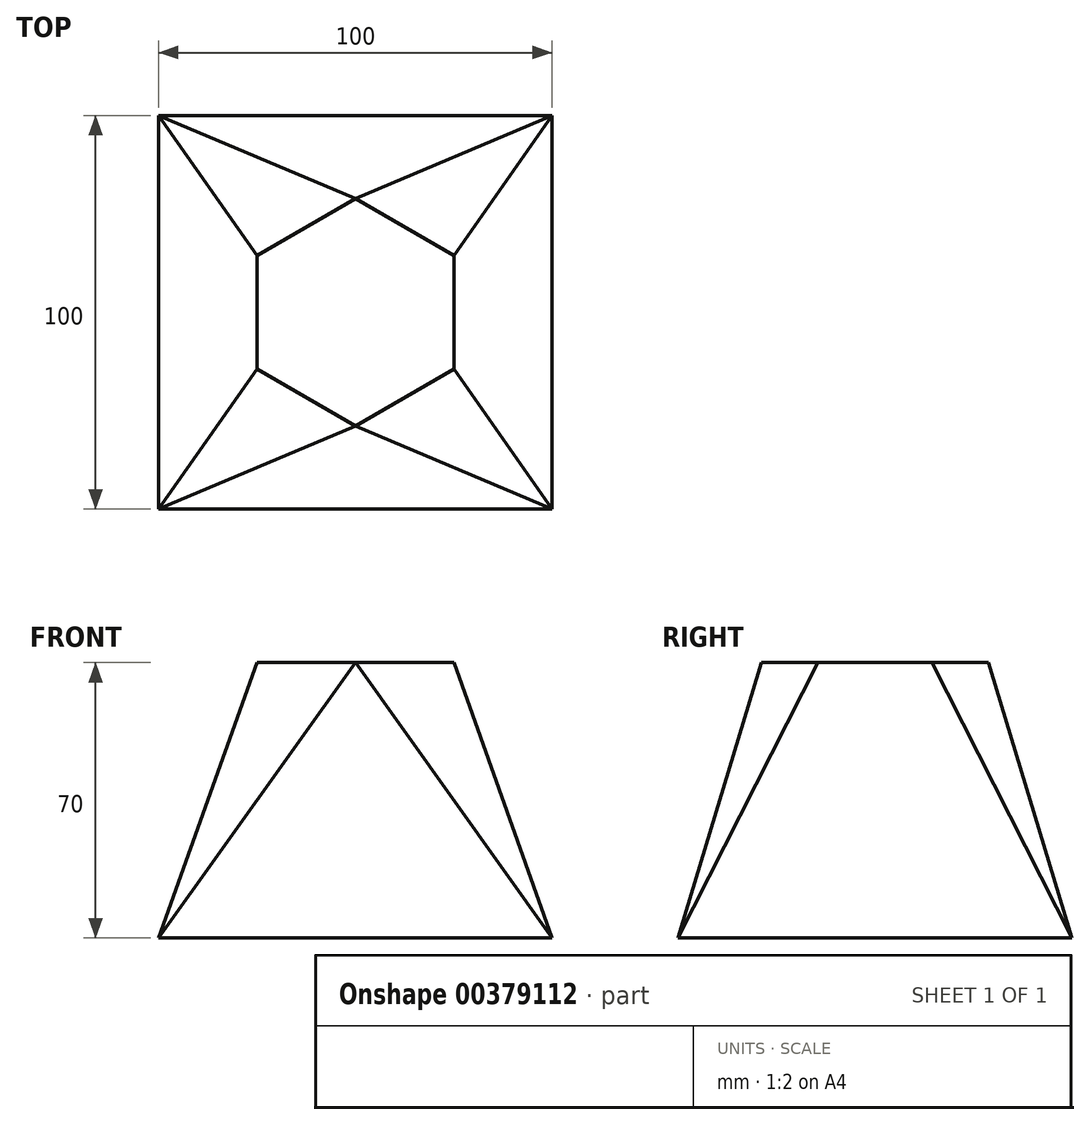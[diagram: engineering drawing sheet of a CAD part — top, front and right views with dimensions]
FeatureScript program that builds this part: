
annotation { "Feature Type Name" : "Feature", "Feature Type Description" : "" }
export const myFeature = defineFeature(function(context is Context, id is Id, definition is map)
    precondition{}
    {
        {
            var Q0;
            Q0=qCreatedBy(makeId("Top.planeOp"),FACE);
            var sketch = newSketch(context, id + "F0", { "sketchPlane" : qUnion([Q0])});
            skLineSegment(sketch, "E0.bottom", {"start": v(50, 50) * mm, "end": v(-50, 50) * mm});
            skLineSegment(sketch, "E0.top", {"start": v(50, -50) * mm, "end": v(-50, -50) * mm});
            skLineSegment(sketch, "E0.left", {"start": v(50, 50) * mm, "end": v(50, -50) * mm});
            skLineSegment(sketch, "E0.right", {"start": v(-50, 50) * mm, "end": v(-50, -50) * mm});
            skPoint(sketch, "E0.middle", {"position": v(0, 0) * mm});
            skSolve(sketch);
        }
        {
            var Q0;
            Q0=qCreatedBy(makeId("Top.planeOp"),FACE);
            cPlane(context, id + "F1", {"entities" : qUnion([Q0]), "cplaneType" : CPlaneType.OFFSET, "offset" : 70 * mm, "width" : 150 * mm, "height" : 150 * mm});
        }
        {
            var Q0;
            Q0=qCreatedBy(id+"F1.planeOp",FACE);
            var sketch = newSketch(context, id + "F2", { "sketchPlane" : qUnion([Q0])});
            skCircle(sketch, "E1.cCircle", {"center": v(0, 0) * mm, "radius": 28.87 * mm, "construction": true});
            skLineSegment(sketch, "E1.0", {"start": v(0, -28.87) * mm, "end": v(-25, -14.43) * mm});
            skLineSegment(sketch, "E1.1", {"start": v(-25, -14.43) * mm, "end": v(-25, 14.43) * mm});
            skLineSegment(sketch, "E1.2", {"start": v(-25, 14.43) * mm, "end": v(0, 28.87) * mm});
            skLineSegment(sketch, "E1.3", {"start": v(0, 28.87) * mm, "end": v(25, 14.43) * mm});
            skLineSegment(sketch, "E1.4", {"start": v(25, 14.43) * mm, "end": v(25, -14.43) * mm});
            skLineSegment(sketch, "E1.5", {"start": v(25, -14.43) * mm, "end": v(0, -28.87) * mm});
            skSolve(sketch);
        }
        {
            var Q0;
            Q0=qCreatedBy(id+"F1.planeOp",FACE);
            var sketch = newSketch(context, id + "F3", { "sketchPlane" : qUnion([Q0])});
            skLineSegment(sketch, "E2.bottom", {"start": v(25, 28.87) * mm, "end": v(-25, 28.87) * mm});
            skLineSegment(sketch, "E2.top", {"start": v(25, -28.87) * mm, "end": v(-25, -28.87) * mm});
            skLineSegment(sketch, "E2.left", {"start": v(25, 28.87) * mm, "end": v(25, -28.87) * mm});
            skLineSegment(sketch, "E2.right", {"start": v(-25, 28.87) * mm, "end": v(-25, -28.87) * mm});
            skSolve(sketch);
        }
        {
            var Q0;
            Q0=makeQuery(id+"F0.imprint","IMPRINT",FACE,{"disambiguationData":[TD([[makeQuery(id+"F0.imprint","IMPRINT",EDGE,{"derivedFrom":sQuery(id+"F0.wireOp",EDGE,"E0.bottom")}),1.0]])]});
            var Q1;
            Q1=makeQuery(id+"F3.imprint","IMPRINT",FACE,{"disambiguationData":[TD([[makeQuery(id+"F3.imprint","IMPRINT",EDGE,{"derivedFrom":sQuery(id+"F3.wireOp",EDGE,"E2.bottom")}),1.0]])]});
            loft(context, id + "F4", {"sheetProfilesArray" : [{ "sheetProfileEntities" : qUnion([Q0]) }, { "sheetProfileEntities" : qUnion([Q1]) }]});
        }
        {
            var Q0;
            Q0=makeQuery(id+"F2.imprint","IMPRINT",FACE,{"disambiguationData":[TD([[makeQuery(id+"F2.imprint","IMPRINT",EDGE,{"derivedFrom":sQuery(id+"F2.wireOp",EDGE,"E1.0")}),-1.0]])]});
            var sketch = newSketch(context, id + "F5", { "sketchPlane" : qUnion([Q0])});
            skLineSegment(sketch, "E3", {"start": v(25, -14.43) * mm, "end": v(0, -28.87) * mm});
            skLineSegment(sketch, "E4", {"start": v(0, -28.87) * mm, "end": v(25, -28.87) * mm});
            skLineSegment(sketch, "E5", {"start": v(25, -28.87) * mm, "end": v(25, -14.43) * mm});
            skSolve(sketch);
        }
        {
            var Q1;
            Q1=makeQuery(id+"F5.imprint","IMPRINT",FACE,{"disambiguationData":[TD([[makeQuery(id+"F5.imprint","IMPRINT",EDGE,{"derivedFrom":sQuery(id+"F5.wireOp",EDGE,"E3")}),1.0]])]});
            var Q2;
            Q2=makeQuery(id+"F4.opLoft","MID_CAP_VERTEX",VERTEX,{"disambiguationData":[OSD([sQuery(id+"F0.wireOp",EDGE,"E0.top"),sQuery(id+"F0.wireOp",EDGE,"E0.left")])],"capPos":0.0});
            loft(context, id + "F6", {"sheetProfilesArray" : [{ "sheetProfileEntities" : qUnion([Q1]) }, { "sheetProfileEntities" : qUnion([Q2]) }]});
        }
        {
            var Q0;
            Q0=makeQuery(id+"F6.opLoft","SWEPT_BODY",BODY,{"disambiguationData":[OSD([sQuery(id+"F0.wireOp",EDGE,"E0.top"),sQuery(id+"F0.wireOp",EDGE,"E0.left"),makeQuery(id+"F5.imprint","IMPRINT",FACE,{"disambiguationData":[TD([[makeQuery(id+"F5.imprint","IMPRINT",EDGE,{"derivedFrom":sQuery(id+"F5.wireOp",EDGE,"E3")}),1.0]])]})])]});
            var Q1;
            Q1=qCreatedBy(makeId("Front.planeOp"),FACE);
            mirror(context, id + "F7", {"entities" : qUnion([Q0]), "mirrorPlane" : qUnion([Q1])});
        }
        {
            var Q0;
            Q0=makeQuery(id+"F7.opPattern","COPY",BODY,{"derivedFrom":makeQuery(id+"F6.opLoft","SWEPT_BODY",BODY,{"disambiguationData":[OSD([sQuery(id+"F0.wireOp",EDGE,"E0.top"),sQuery(id+"F0.wireOp",EDGE,"E0.left"),makeQuery(id+"F5.imprint","IMPRINT",FACE,{"disambiguationData":[TD([[makeQuery(id+"F5.imprint","IMPRINT",EDGE,{"derivedFrom":sQuery(id+"F5.wireOp",EDGE,"E3")}),1.0]])]})])]}),"instanceName":"1"});
            var Q1;
            Q1=qCreatedBy(makeId("Right.planeOp"),FACE);
            mirror(context, id + "F8", {"entities" : qUnion([Q0]), "mirrorPlane" : qUnion([Q1])});
        }
        {
            var Q0;
            Q0=makeQuery(id+"F8.opPattern","COPY",BODY,{"derivedFrom":makeQuery(id+"F7.opPattern","COPY",BODY,{"derivedFrom":makeQuery(id+"F6.opLoft","SWEPT_BODY",BODY,{"disambiguationData":[OSD([sQuery(id+"F0.wireOp",EDGE,"E0.top"),sQuery(id+"F0.wireOp",EDGE,"E0.left"),makeQuery(id+"F5.imprint","IMPRINT",FACE,{"disambiguationData":[TD([[makeQuery(id+"F5.imprint","IMPRINT",EDGE,{"derivedFrom":sQuery(id+"F5.wireOp",EDGE,"E3")}),1.0]])]})])]}),"instanceName":"1"}),"instanceName":"1"});
            var Q1;
            Q1=qCreatedBy(makeId("Front.planeOp"),FACE);
            mirror(context, id + "F9", {"entities" : qUnion([Q0]), "mirrorPlane" : qUnion([Q1])});
        }
        {
            var Q0;
            Q0=makeQuery(id+"F6.opLoft","SWEPT_BODY",BODY,{"disambiguationData":[OSD([sQuery(id+"F0.wireOp",EDGE,"E0.top"),sQuery(id+"F0.wireOp",EDGE,"E0.left"),makeQuery(id+"F5.imprint","IMPRINT",FACE,{"disambiguationData":[TD([[makeQuery(id+"F5.imprint","IMPRINT",EDGE,{"derivedFrom":sQuery(id+"F5.wireOp",EDGE,"E3")}),1.0]])]})])]});
            var Q1;
            Q1=makeQuery(id+"F4.opLoft","SWEPT_BODY",BODY,{"disambiguationData":[OSD([makeQuery(id+"F0.imprint","IMPRINT",FACE,{"disambiguationData":[TD([[makeQuery(id+"F0.imprint","IMPRINT",EDGE,{"derivedFrom":sQuery(id+"F0.wireOp",EDGE,"E0.bottom")}),1.0]])]}),makeQuery(id+"F3.imprint","IMPRINT",FACE,{"disambiguationData":[TD([[makeQuery(id+"F3.imprint","IMPRINT",EDGE,{"derivedFrom":sQuery(id+"F3.wireOp",EDGE,"E2.bottom")}),1.0]])]})])]});
            booleanBodies(context, id + "F10", {"operationType" : BooleanOperationType.SUBTRACTION, "tools" : qUnion([Q0]), "targets" : qUnion([Q1])});
        }
        {
            var Q0;
            Q0=makeQuery(id+"F7.opPattern","COPY",BODY,{"derivedFrom":makeQuery(id+"F6.opLoft","SWEPT_BODY",BODY,{"disambiguationData":[OSD([sQuery(id+"F0.wireOp",EDGE,"E0.top"),sQuery(id+"F0.wireOp",EDGE,"E0.left"),makeQuery(id+"F5.imprint","IMPRINT",FACE,{"disambiguationData":[TD([[makeQuery(id+"F5.imprint","IMPRINT",EDGE,{"derivedFrom":sQuery(id+"F5.wireOp",EDGE,"E3")}),1.0]])]})])]}),"instanceName":"1"});
            var Q1;
            Q1=makeQuery(id+"F4.opLoft","SWEPT_BODY",BODY,{"disambiguationData":[OSD([makeQuery(id+"F0.imprint","IMPRINT",FACE,{"disambiguationData":[TD([[makeQuery(id+"F0.imprint","IMPRINT",EDGE,{"derivedFrom":sQuery(id+"F0.wireOp",EDGE,"E0.bottom")}),1.0]])]}),makeQuery(id+"F3.imprint","IMPRINT",FACE,{"disambiguationData":[TD([[makeQuery(id+"F3.imprint","IMPRINT",EDGE,{"derivedFrom":sQuery(id+"F3.wireOp",EDGE,"E2.bottom")}),1.0]])]})])]});
            booleanBodies(context, id + "F11", {"operationType" : BooleanOperationType.SUBTRACTION, "tools" : qUnion([Q0]), "targets" : qUnion([Q1])});
        }
        {
            var Q0;
            Q0=makeQuery(id+"F8.opPattern","COPY",BODY,{"derivedFrom":makeQuery(id+"F7.opPattern","COPY",BODY,{"derivedFrom":makeQuery(id+"F6.opLoft","SWEPT_BODY",BODY,{"disambiguationData":[OSD([sQuery(id+"F0.wireOp",EDGE,"E0.top"),sQuery(id+"F0.wireOp",EDGE,"E0.left"),makeQuery(id+"F5.imprint","IMPRINT",FACE,{"disambiguationData":[TD([[makeQuery(id+"F5.imprint","IMPRINT",EDGE,{"derivedFrom":sQuery(id+"F5.wireOp",EDGE,"E3")}),1.0]])]})])]}),"instanceName":"1"}),"instanceName":"1"});
            var Q1;
            Q1=makeQuery(id+"F4.opLoft","SWEPT_BODY",BODY,{"disambiguationData":[OSD([makeQuery(id+"F0.imprint","IMPRINT",FACE,{"disambiguationData":[TD([[makeQuery(id+"F0.imprint","IMPRINT",EDGE,{"derivedFrom":sQuery(id+"F0.wireOp",EDGE,"E0.bottom")}),1.0]])]}),makeQuery(id+"F3.imprint","IMPRINT",FACE,{"disambiguationData":[TD([[makeQuery(id+"F3.imprint","IMPRINT",EDGE,{"derivedFrom":sQuery(id+"F3.wireOp",EDGE,"E2.bottom")}),1.0]])]})])]});
            booleanBodies(context, id + "F12", {"operationType" : BooleanOperationType.SUBTRACTION, "tools" : qUnion([Q0]), "targets" : qUnion([Q1])});
        }
        {
            var Q0;
            Q0=makeQuery(id+"F9.opPattern","COPY",BODY,{"derivedFrom":makeQuery(id+"F8.opPattern","COPY",BODY,{"derivedFrom":makeQuery(id+"F7.opPattern","COPY",BODY,{"derivedFrom":makeQuery(id+"F6.opLoft","SWEPT_BODY",BODY,{"disambiguationData":[OSD([sQuery(id+"F0.wireOp",EDGE,"E0.top"),sQuery(id+"F0.wireOp",EDGE,"E0.left"),makeQuery(id+"F5.imprint","IMPRINT",FACE,{"disambiguationData":[TD([[makeQuery(id+"F5.imprint","IMPRINT",EDGE,{"derivedFrom":sQuery(id+"F5.wireOp",EDGE,"E3")}),1.0]])]})])]}),"instanceName":"1"}),"instanceName":"1"}),"instanceName":"1"});
            var Q1;
            Q1=makeQuery(id+"F4.opLoft","SWEPT_BODY",BODY,{"disambiguationData":[OSD([makeQuery(id+"F0.imprint","IMPRINT",FACE,{"disambiguationData":[TD([[makeQuery(id+"F0.imprint","IMPRINT",EDGE,{"derivedFrom":sQuery(id+"F0.wireOp",EDGE,"E0.bottom")}),1.0]])]}),makeQuery(id+"F3.imprint","IMPRINT",FACE,{"disambiguationData":[TD([[makeQuery(id+"F3.imprint","IMPRINT",EDGE,{"derivedFrom":sQuery(id+"F3.wireOp",EDGE,"E2.bottom")}),1.0]])]})])]});
            booleanBodies(context, id + "F13", {"operationType" : BooleanOperationType.SUBTRACTION, "tools" : qUnion([Q0]), "targets" : qUnion([Q1])});
        }
    });
